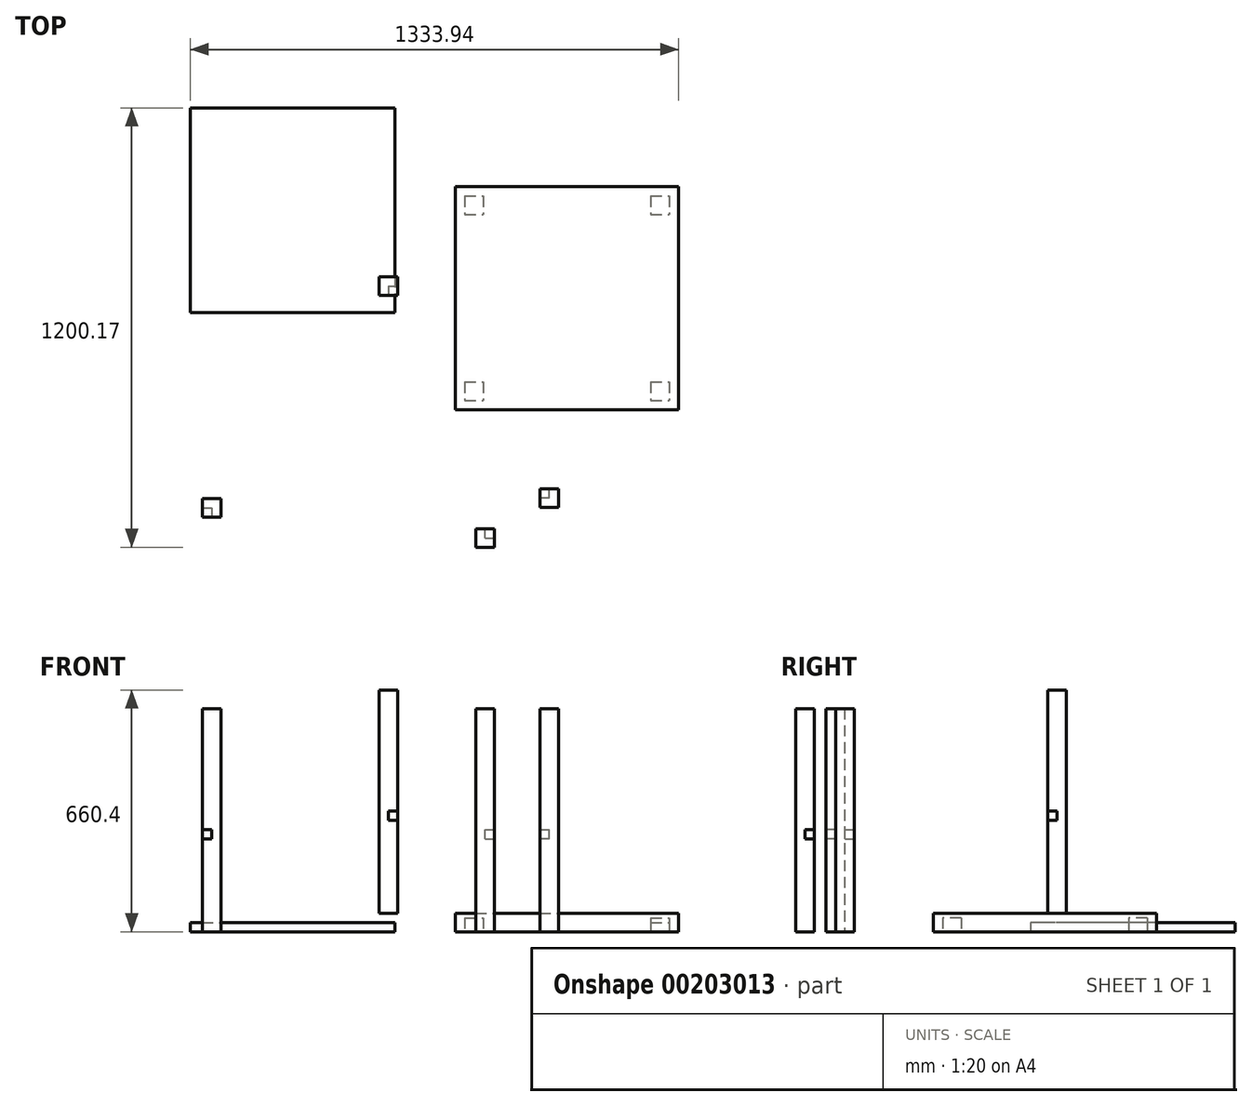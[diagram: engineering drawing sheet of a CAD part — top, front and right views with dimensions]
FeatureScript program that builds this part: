
annotation { "Feature Type Name" : "Feature", "Feature Type Description" : "" }
export const myFeature = defineFeature(function(context is Context, id is Id, definition is map)
    precondition{}
    {
        {
            var Q0;
            Q0=qCreatedBy(makeId("Top.planeOp"),FACE);
            var sketch = newSketch(context, id + "F0", { "sketchPlane" : qUnion([Q0])});
            skLineSegment(sketch, "E0.bottom", {"start": v(-297.35, 431.95) * mm, "end": v(312.25, 431.95) * mm});
            skLineSegment(sketch, "E0.top", {"start": v(-297.35, -177.65) * mm, "end": v(312.25, -177.65) * mm});
            skLineSegment(sketch, "E0.left", {"start": v(-297.35, 431.95) * mm, "end": v(-297.35, -177.65) * mm});
            skLineSegment(sketch, "E0.right", {"start": v(312.25, 431.95) * mm, "end": v(312.25, -177.65) * mm});
            skLineSegment(sketch, "E1.0", {"start": v(-297.35, 406.55) * mm, "end": v(312.25, 406.55) * mm});
            skLineSegment(sketch, "E2.0", {"start": v(286.85, 431.95) * mm, "end": v(286.85, -177.65) * mm});
            skLineSegment(sketch, "E3.0", {"start": v(-297.35, -152.25) * mm, "end": v(312.25, -152.25) * mm});
            skLineSegment(sketch, "E4.0", {"start": v(-271.95, 431.95) * mm, "end": v(-271.95, -177.65) * mm});
            skLineSegment(sketch, "E5.0", {"start": v(-297.35, 355.75) * mm, "end": v(312.25, 355.75) * mm});
            skLineSegment(sketch, "E6.0", {"start": v(236.05, 431.95) * mm, "end": v(236.05, -177.65) * mm});
            skLineSegment(sketch, "E7.0", {"start": v(-297.35, -101.45) * mm, "end": v(312.25, -101.45) * mm});
            skLineSegment(sketch, "E8.0", {"start": v(-221.15, 431.95) * mm, "end": v(-221.15, -177.65) * mm});
            skSolve(sketch);
        }
        {
            var Q0;
            {var subQ0=sQuery(id+"F0.wireOp",EDGE,"E0.left");var subQ1=sQuery(id+"F0.wireOp",EDGE,"E0.bottom");var subQ2=makeQuery(id+"F0.imprint","INTERSECT",VERTEX,{"derivedFrom":[subQ1,subQ0]});Q0=makeQuery(id+"F0.imprint","IMPRINT",FACE,{"disambiguationData":[TD([[makeQuery(id+"F0.imprint","IMPRINT",EDGE,{"disambiguationData":[TD([[subQ2,-1.0]])],"derivedFrom":subQ1}),-1.0]])]});}
            var Q1;
            {var subQ0=sQuery(id+"F0.wireOp",EDGE,"E0.right");var subQ1=sQuery(id+"F0.wireOp",EDGE,"E0.bottom");var subQ2=makeQuery(id+"F0.imprint","INTERSECT",VERTEX,{"derivedFrom":[subQ1,subQ0]});Q1=makeQuery(id+"F0.imprint","IMPRINT",FACE,{"disambiguationData":[TD([[makeQuery(id+"F0.imprint","IMPRINT",EDGE,{"disambiguationData":[TD([[subQ2,1.0]])],"derivedFrom":subQ1}),-1.0]])]});}
            var Q2;
            {var subQ0=sQuery(id+"F0.wireOp",EDGE,"E0.left");var subQ1=sQuery(id+"F0.wireOp",EDGE,"E0.top");var subQ2=makeQuery(id+"F0.imprint","INTERSECT",VERTEX,{"derivedFrom":[subQ1,subQ0]});Q2=makeQuery(id+"F0.imprint","IMPRINT",FACE,{"disambiguationData":[TD([[makeQuery(id+"F0.imprint","IMPRINT",EDGE,{"disambiguationData":[TD([[subQ2,-1.0]])],"derivedFrom":subQ1}),1.0]])]});}
            var Q3;
            {var subQ0=sQuery(id+"F0.wireOp",EDGE,"E0.right");var subQ1=sQuery(id+"F0.wireOp",EDGE,"E0.top");var subQ2=makeQuery(id+"F0.imprint","INTERSECT",VERTEX,{"derivedFrom":[subQ1,subQ0]});Q3=makeQuery(id+"F0.imprint","IMPRINT",FACE,{"disambiguationData":[TD([[makeQuery(id+"F0.imprint","IMPRINT",EDGE,{"disambiguationData":[TD([[subQ2,1.0]])],"derivedFrom":subQ1}),1.0]])]});}
            var Q4;
            {var subQ0=sQuery(id+"F0.wireOp",EDGE,"E4.0");var subQ1=sQuery(id+"F0.wireOp",EDGE,"E0.bottom");var subQ2=makeQuery(id+"F0.imprint","INTERSECT",VERTEX,{"derivedFrom":[subQ1,subQ0]});Q4=makeQuery(id+"F0.imprint","IMPRINT",FACE,{"disambiguationData":[TD([[makeQuery(id+"F0.imprint","IMPRINT",EDGE,{"disambiguationData":[TD([[subQ2,-1.0]])],"derivedFrom":subQ1}),-1.0]])]});}
            var Q5;
            {var subQ0=sQuery(id+"F0.wireOp",EDGE,"E6.0");var subQ1=sQuery(id+"F0.wireOp",EDGE,"E0.bottom");var subQ2=makeQuery(id+"F0.imprint","INTERSECT",VERTEX,{"derivedFrom":[subQ1,subQ0]});Q5=makeQuery(id+"F0.imprint","IMPRINT",FACE,{"disambiguationData":[TD([[makeQuery(id+"F0.imprint","IMPRINT",EDGE,{"disambiguationData":[TD([[subQ2,1.0]])],"derivedFrom":subQ1}),-1.0]])]});}
            var Q6;
            {var subQ0=sQuery(id+"F0.wireOp",EDGE,"E2.0");var subQ1=sQuery(id+"F0.wireOp",EDGE,"E0.bottom");var subQ2=makeQuery(id+"F0.imprint","INTERSECT",VERTEX,{"derivedFrom":[subQ1,subQ0]});Q6=makeQuery(id+"F0.imprint","IMPRINT",FACE,{"disambiguationData":[TD([[makeQuery(id+"F0.imprint","IMPRINT",EDGE,{"disambiguationData":[TD([[subQ2,1.0]])],"derivedFrom":subQ1}),-1.0]])]});}
            var Q7;
            {var subQ0=sQuery(id+"F0.wireOp",EDGE,"E4.0");var subQ1=sQuery(id+"F0.wireOp",EDGE,"E0.top");var subQ2=makeQuery(id+"F0.imprint","INTERSECT",VERTEX,{"derivedFrom":[subQ1,subQ0]});Q7=makeQuery(id+"F0.imprint","IMPRINT",FACE,{"disambiguationData":[TD([[makeQuery(id+"F0.imprint","IMPRINT",EDGE,{"disambiguationData":[TD([[subQ2,-1.0]])],"derivedFrom":subQ1}),1.0]])]});}
            var Q8;
            {var subQ0=sQuery(id+"F0.wireOp",EDGE,"E6.0");var subQ1=sQuery(id+"F0.wireOp",EDGE,"E0.top");var subQ2=makeQuery(id+"F0.imprint","INTERSECT",VERTEX,{"derivedFrom":[subQ1,subQ0]});Q8=makeQuery(id+"F0.imprint","IMPRINT",FACE,{"disambiguationData":[TD([[makeQuery(id+"F0.imprint","IMPRINT",EDGE,{"disambiguationData":[TD([[subQ2,1.0]])],"derivedFrom":subQ1}),1.0]])]});}
            var Q9;
            {var subQ0=sQuery(id+"F0.wireOp",EDGE,"E2.0");var subQ1=sQuery(id+"F0.wireOp",EDGE,"E0.top");var subQ2=makeQuery(id+"F0.imprint","INTERSECT",VERTEX,{"derivedFrom":[subQ1,subQ0]});Q9=makeQuery(id+"F0.imprint","IMPRINT",FACE,{"disambiguationData":[TD([[makeQuery(id+"F0.imprint","IMPRINT",EDGE,{"disambiguationData":[TD([[subQ2,1.0]])],"derivedFrom":subQ1}),1.0]])]});}
            var Q10;
            {var subQ0=sQuery(id+"F0.wireOp",EDGE,"E1.0");var subQ1=sQuery(id+"F0.wireOp",EDGE,"E0.left");var subQ2=makeQuery(id+"F0.imprint","INTERSECT",VERTEX,{"derivedFrom":[subQ1,subQ0]});Q10=makeQuery(id+"F0.imprint","IMPRINT",FACE,{"disambiguationData":[TD([[makeQuery(id+"F0.imprint","IMPRINT",EDGE,{"disambiguationData":[TD([[subQ2,-1.0]])],"derivedFrom":subQ1}),1.0]])]});}
            var Q11;
            {var subQ0=sQuery(id+"F0.wireOp",EDGE,"E5.0");var subQ1=sQuery(id+"F0.wireOp",EDGE,"E0.left");var subQ2=makeQuery(id+"F0.imprint","INTERSECT",VERTEX,{"derivedFrom":[subQ1,subQ0]});Q11=makeQuery(id+"F0.imprint","IMPRINT",FACE,{"disambiguationData":[TD([[makeQuery(id+"F0.imprint","IMPRINT",EDGE,{"disambiguationData":[TD([[subQ2,-1.0]])],"derivedFrom":subQ1}),1.0]])]});}
            var Q12;
            {var subQ0=sQuery(id+"F0.wireOp",EDGE,"E3.0");var subQ1=sQuery(id+"F0.wireOp",EDGE,"E0.left");var subQ2=makeQuery(id+"F0.imprint","INTERSECT",VERTEX,{"derivedFrom":[subQ1,subQ0]});Q12=makeQuery(id+"F0.imprint","IMPRINT",FACE,{"disambiguationData":[TD([[makeQuery(id+"F0.imprint","IMPRINT",EDGE,{"disambiguationData":[TD([[subQ2,1.0]])],"derivedFrom":subQ1}),1.0]])]});}
            var Q13;
            {var subQ0=sQuery(id+"F0.wireOp",EDGE,"E1.0");var subQ1=sQuery(id+"F0.wireOp",EDGE,"E0.right");var subQ2=makeQuery(id+"F0.imprint","INTERSECT",VERTEX,{"derivedFrom":[subQ1,subQ0]});Q13=makeQuery(id+"F0.imprint","IMPRINT",FACE,{"disambiguationData":[TD([[makeQuery(id+"F0.imprint","IMPRINT",EDGE,{"disambiguationData":[TD([[subQ2,-1.0]])],"derivedFrom":subQ1}),-1.0]])]});}
            var Q14;
            {var subQ0=sQuery(id+"F0.wireOp",EDGE,"E5.0");var subQ1=sQuery(id+"F0.wireOp",EDGE,"E0.right");var subQ2=makeQuery(id+"F0.imprint","INTERSECT",VERTEX,{"derivedFrom":[subQ1,subQ0]});Q14=makeQuery(id+"F0.imprint","IMPRINT",FACE,{"disambiguationData":[TD([[makeQuery(id+"F0.imprint","IMPRINT",EDGE,{"disambiguationData":[TD([[subQ2,-1.0]])],"derivedFrom":subQ1}),-1.0]])]});}
            var Q15;
            {var subQ0=sQuery(id+"F0.wireOp",EDGE,"E3.0");var subQ1=sQuery(id+"F0.wireOp",EDGE,"E0.right");var subQ2=makeQuery(id+"F0.imprint","INTERSECT",VERTEX,{"derivedFrom":[subQ1,subQ0]});Q15=makeQuery(id+"F0.imprint","IMPRINT",FACE,{"disambiguationData":[TD([[makeQuery(id+"F0.imprint","IMPRINT",EDGE,{"disambiguationData":[TD([[subQ2,1.0]])],"derivedFrom":subQ1}),-1.0]])]});}
            var Q16;
            {var subQ0=sQuery(id+"F0.wireOp",EDGE,"E5.0");var subQ1=sQuery(id+"F0.wireOp",EDGE,"E4.0");var subQ2=makeQuery(id+"F0.imprint","INTERSECT",VERTEX,{"derivedFrom":[subQ1,subQ0]});Q16=makeQuery(id+"F0.imprint","IMPRINT",FACE,{"disambiguationData":[TD([[makeQuery(id+"F0.imprint","IMPRINT",EDGE,{"disambiguationData":[TD([[subQ2,-1.0]])],"derivedFrom":subQ1}),1.0]])]});}
            var Q17;
            {var subQ0=sQuery(id+"F0.wireOp",EDGE,"E8.0");var subQ1=sQuery(id+"F0.wireOp",EDGE,"E1.0");var subQ2=makeQuery(id+"F0.imprint","INTERSECT",VERTEX,{"derivedFrom":[subQ1,subQ0]});Q17=makeQuery(id+"F0.imprint","IMPRINT",FACE,{"disambiguationData":[TD([[makeQuery(id+"F0.imprint","IMPRINT",EDGE,{"disambiguationData":[TD([[subQ2,-1.0]])],"derivedFrom":subQ1}),-1.0]])]});}
            var Q18;
            {var subQ0=sQuery(id+"F0.wireOp",EDGE,"E5.0");var subQ1=sQuery(id+"F0.wireOp",EDGE,"E2.0");var subQ2=makeQuery(id+"F0.imprint","INTERSECT",VERTEX,{"derivedFrom":[subQ1,subQ0]});Q18=makeQuery(id+"F0.imprint","IMPRINT",FACE,{"disambiguationData":[TD([[makeQuery(id+"F0.imprint","IMPRINT",EDGE,{"disambiguationData":[TD([[subQ2,-1.0]])],"derivedFrom":subQ1}),-1.0]])]});}
            var Q19;
            {var subQ0=sQuery(id+"F0.wireOp",EDGE,"E4.0");var subQ1=sQuery(id+"F0.wireOp",EDGE,"E1.0");var subQ2=makeQuery(id+"F0.imprint","INTERSECT",VERTEX,{"derivedFrom":[subQ1,subQ0]});Q19=makeQuery(id+"F0.imprint","IMPRINT",FACE,{"disambiguationData":[TD([[makeQuery(id+"F0.imprint","IMPRINT",EDGE,{"disambiguationData":[TD([[subQ2,-1.0]])],"derivedFrom":subQ1}),-1.0]])]});}
            var Q20;
            {var subQ0=sQuery(id+"F0.wireOp",EDGE,"E4.0");var subQ1=sQuery(id+"F0.wireOp",EDGE,"E3.0");var subQ2=makeQuery(id+"F0.imprint","INTERSECT",VERTEX,{"derivedFrom":[subQ1,subQ0]});Q20=makeQuery(id+"F0.imprint","IMPRINT",FACE,{"disambiguationData":[TD([[makeQuery(id+"F0.imprint","IMPRINT",EDGE,{"disambiguationData":[TD([[subQ2,-1.0]])],"derivedFrom":subQ1}),1.0]])]});}
            var Q21;
            {var subQ0=sQuery(id+"F0.wireOp",EDGE,"E8.0");var subQ1=sQuery(id+"F0.wireOp",EDGE,"E5.0");var subQ2=makeQuery(id+"F0.imprint","INTERSECT",VERTEX,{"derivedFrom":[subQ1,subQ0]});Q21=makeQuery(id+"F0.imprint","IMPRINT",FACE,{"disambiguationData":[TD([[makeQuery(id+"F0.imprint","IMPRINT",EDGE,{"disambiguationData":[TD([[subQ2,-1.0]])],"derivedFrom":subQ1}),-1.0]])]});}
            var Q22;
            {var subQ0=sQuery(id+"F0.wireOp",EDGE,"E8.0");var subQ1=sQuery(id+"F0.wireOp",EDGE,"E3.0");var subQ2=makeQuery(id+"F0.imprint","INTERSECT",VERTEX,{"derivedFrom":[subQ1,subQ0]});Q22=makeQuery(id+"F0.imprint","IMPRINT",FACE,{"disambiguationData":[TD([[makeQuery(id+"F0.imprint","IMPRINT",EDGE,{"disambiguationData":[TD([[subQ2,-1.0]])],"derivedFrom":subQ1}),1.0]])]});}
            var Q23;
            {var subQ0=sQuery(id+"F0.wireOp",EDGE,"E7.0");var subQ1=sQuery(id+"F0.wireOp",EDGE,"E2.0");var subQ2=makeQuery(id+"F0.imprint","INTERSECT",VERTEX,{"derivedFrom":[subQ1,subQ0]});Q23=makeQuery(id+"F0.imprint","IMPRINT",FACE,{"disambiguationData":[TD([[makeQuery(id+"F0.imprint","IMPRINT",EDGE,{"disambiguationData":[TD([[subQ2,-1.0]])],"derivedFrom":subQ1}),-1.0]])]});}
            var Q24;
            {var subQ0=sQuery(id+"F0.wireOp",EDGE,"E6.0");var subQ1=sQuery(id+"F0.wireOp",EDGE,"E1.0");var subQ2=makeQuery(id+"F0.imprint","INTERSECT",VERTEX,{"derivedFrom":[subQ1,subQ0]});Q24=makeQuery(id+"F0.imprint","IMPRINT",FACE,{"disambiguationData":[TD([[makeQuery(id+"F0.imprint","IMPRINT",EDGE,{"disambiguationData":[TD([[subQ2,-1.0]])],"derivedFrom":subQ1}),-1.0]])]});}
            extrude(context, id + "F1", {"entities" : qUnion([Q0, Q1, Q2, Q3, Q4, Q5, Q6, Q7, Q8, Q9, Q10, Q11, Q12, Q13, Q14, Q15, Q16, Q17, Q18, Q19, Q20, Q21, Q22, Q23, Q24]), "depth" : 50.8 * mm});
        }
        {
            var Q0;
            {var subQ0=sQuery(id+"F0.wireOp",EDGE,"E4.0");var subQ1=sQuery(id+"F0.wireOp",EDGE,"E3.0");var subQ2=makeQuery(id+"F0.imprint","INTERSECT",VERTEX,{"derivedFrom":[subQ1,subQ0]});Q0=makeQuery(id+"F0.imprint","IMPRINT",FACE,{"disambiguationData":[TD([[makeQuery(id+"F0.imprint","IMPRINT",EDGE,{"disambiguationData":[TD([[subQ2,-1.0]])],"derivedFrom":subQ1}),1.0]])]});}
            extrude(context, id + "F2", {"entities" : qUnion([Q0]), "operationType" : NewBodyOperationType.REMOVE, "oppositeDirection" : true, "depth" : 38.1 * mm});
        }
        {
            var Q0;
            {var subQ0=sQuery(id+"F0.wireOp",EDGE,"E4.0");var subQ1=sQuery(id+"F0.wireOp",EDGE,"E3.0");var subQ2=makeQuery(id+"F0.imprint","INTERSECT",VERTEX,{"derivedFrom":[subQ1,subQ0]});Q0=makeQuery(id+"F0.imprint","IMPRINT",FACE,{"disambiguationData":[TD([[makeQuery(id+"F0.imprint","IMPRINT",EDGE,{"disambiguationData":[TD([[subQ2,-1.0]])],"derivedFrom":subQ1}),1.0]])]});}
            extrude(context, id + "F3", {"entities" : qUnion([Q0]), "operationType" : NewBodyOperationType.REMOVE, "depth" : 38.1 * mm});
        }
        {
            var Q0;
            {var subQ0=sQuery(id+"F0.wireOp",EDGE,"E7.0");var subQ1=sQuery(id+"F0.wireOp",EDGE,"E2.0");var subQ2=makeQuery(id+"F0.imprint","INTERSECT",VERTEX,{"derivedFrom":[subQ1,subQ0]});Q0=makeQuery(id+"F0.imprint","IMPRINT",FACE,{"disambiguationData":[TD([[makeQuery(id+"F0.imprint","IMPRINT",EDGE,{"disambiguationData":[TD([[subQ2,-1.0]])],"derivedFrom":subQ1}),-1.0]])]});}
            extrude(context, id + "F4", {"entities" : qUnion([Q0]), "operationType" : NewBodyOperationType.REMOVE, "depth" : 38.1 * mm});
        }
        {
            var Q0;
            {var subQ0=sQuery(id+"F0.wireOp",EDGE,"E4.0");var subQ1=sQuery(id+"F0.wireOp",EDGE,"E1.0");var subQ2=makeQuery(id+"F0.imprint","INTERSECT",VERTEX,{"derivedFrom":[subQ1,subQ0]});Q0=makeQuery(id+"F0.imprint","IMPRINT",FACE,{"disambiguationData":[TD([[makeQuery(id+"F0.imprint","IMPRINT",EDGE,{"disambiguationData":[TD([[subQ2,-1.0]])],"derivedFrom":subQ1}),-1.0]])]});}
            extrude(context, id + "F5", {"entities" : qUnion([Q0]), "operationType" : NewBodyOperationType.REMOVE, "depth" : 38.1 * mm});
        }
        {
            var Q0;
            Q0=makeQuery(id+"F1.opExtrude","CAP_FACE",FACE,{"disambiguationData":[OSD([sQuery(id+"F0.wireOp",EDGE,"E0.bottom"),sQuery(id+"F0.wireOp",EDGE,"E0.top"),sQuery(id+"F0.wireOp",EDGE,"E0.left"),sQuery(id+"F0.wireOp",EDGE,"E0.right")])],"isStart":false});
            var sketch = newSketch(context, id + "F6", { "sketchPlane" : qUnion([Q0])});
            skLineSegment(sketch, "E9.bottom", {"start": v(-506.38, 185.9) * mm, "end": v(-455.58, 185.9) * mm});
            skLineSegment(sketch, "E9.top", {"start": v(-506.38, 135.1) * mm, "end": v(-455.58, 135.1) * mm});
            skLineSegment(sketch, "E9.left", {"start": v(-506.38, 185.9) * mm, "end": v(-506.38, 135.1) * mm});
            skLineSegment(sketch, "E9.right", {"start": v(-455.58, 185.9) * mm, "end": v(-455.58, 135.1) * mm});
            skLineSegment(sketch, "E10.0", {"start": v(-506.38, 160.5) * mm, "end": v(-455.58, 160.5) * mm});
            skLineSegment(sketch, "E11.0", {"start": v(-480.98, 185.9) * mm, "end": v(-480.98, 135.1) * mm});
            skSolve(sketch);
        }
        {
            var Q0;
            Q0 = qSketchRegion(id + "F6", true);
            extrude(context, id + "F7", {"entities" : qUnion([Q0]), "depth" : 609.6 * mm});
        }
        {
            var Q0;
            Q0=qCreatedBy(makeId("Top.planeOp"),FACE);
            var sketch = newSketch(context, id + "F8", { "sketchPlane" : qUnion([Q0])});
            skLineSegment(sketch, "E12.bottom", {"start": v(-242.21, -501.92) * mm, "end": v(-191.41, -501.92) * mm});
            skLineSegment(sketch, "E12.top", {"start": v(-242.21, -552.72) * mm, "end": v(-191.41, -552.72) * mm});
            skLineSegment(sketch, "E12.left", {"start": v(-242.21, -501.92) * mm, "end": v(-242.21, -552.72) * mm});
            skLineSegment(sketch, "E12.right", {"start": v(-191.41, -501.92) * mm, "end": v(-191.41, -552.72) * mm});
            skLineSegment(sketch, "E13.0", {"start": v(-242.21, -527.32) * mm, "end": v(-191.41, -527.32) * mm});
            skLineSegment(sketch, "E14.0", {"start": v(-216.81, -501.92) * mm, "end": v(-216.81, -552.72) * mm});
            skSolve(sketch);
        }
        {
            var Q0;
            Q0=makeQuery(id+"F8.imprint","IMPRINT",FACE,{"disambiguationData":[TD([[makeQuery(id+"F8.imprint","IMPRINT",EDGE,{"derivedFrom":sQuery(id+"F8.wireOp",EDGE,"E12.bottom")}),-1.0]])]});
            extrude(context, id + "F9", {"entities" : qUnion([Q0]), "operationType" : NewBodyOperationType.ADD, "depth" : 609.6 * mm});
        }
        {
            var Q0;
            Q0 = qSketchRegion(id + "F8", true);
            extrude(context, id + "F10", {"entities" : qUnion([Q0]), "operationType" : NewBodyOperationType.ADD, "depth" : 609.6 * mm});
        }
        {
            var Q0;
            Q0=qCreatedBy(makeId("Top.planeOp"),FACE);
            var sketch = newSketch(context, id + "F11", { "sketchPlane" : qUnion([Q0])});
            skLineSegment(sketch, "E15.bottom", {"start": v(-989.34, -521.4) * mm, "end": v(-938.54, -521.4) * mm});
            skLineSegment(sketch, "E15.top", {"start": v(-989.34, -470.6) * mm, "end": v(-938.54, -470.6) * mm});
            skLineSegment(sketch, "E15.left", {"start": v(-989.34, -521.4) * mm, "end": v(-989.34, -470.6) * mm});
            skLineSegment(sketch, "E15.right", {"start": v(-938.54, -521.4) * mm, "end": v(-938.54, -470.6) * mm});
            skLineSegment(sketch, "E16.0", {"start": v(-963.94, -521.4) * mm, "end": v(-963.94, -470.6) * mm});
            skLineSegment(sketch, "E17.0", {"start": v(-989.34, -496) * mm, "end": v(-938.54, -496) * mm});
            skSolve(sketch);
        }
        {
            var Q0;
            Q0 = qSketchRegion(id + "F11", true);
            extrude(context, id + "F12", {"entities" : qUnion([Q0]), "operationType" : NewBodyOperationType.ADD, "depth" : 609.6 * mm});
        }
        {
            var Q0;
            Q0=qCreatedBy(makeId("Top.planeOp"),FACE);
            var sketch = newSketch(context, id + "F13", { "sketchPlane" : qUnion([Q0])});
            skLineSegment(sketch, "E18.bottom", {"start": v(-31.1, -378.64) * mm, "end": v(19.7, -378.64) * mm});
            skLineSegment(sketch, "E18.top", {"start": v(-31.1, -429.44) * mm, "end": v(19.7, -429.44) * mm});
            skLineSegment(sketch, "E18.left", {"start": v(-31.1, -378.64) * mm, "end": v(-31.1, -429.44) * mm});
            skLineSegment(sketch, "E18.right", {"start": v(19.7, -378.64) * mm, "end": v(19.7, -429.44) * mm});
            skLineSegment(sketch, "E19.0", {"start": v(-31.1, -404.04) * mm, "end": v(19.7, -404.04) * mm});
            skLineSegment(sketch, "E20.0", {"start": v(-5.7, -378.64) * mm, "end": v(-5.7, -429.44) * mm});
            skSolve(sketch);
        }
        {
            var Q0;
            Q0 = qSketchRegion(id + "F13", true);
            extrude(context, id + "F14", {"entities" : qUnion([Q0]), "operationType" : NewBodyOperationType.ADD, "depth" : 609.6 * mm});
        }
        {
            var Q0;
            {var subQ0=sQuery(id+"F13.wireOp",EDGE,"E18.left");var subQ1=sQuery(id+"F13.wireOp",EDGE,"E18.top");var subQ2=makeQuery(id+"F13.imprint","INTERSECT",VERTEX,{"derivedFrom":[subQ1,subQ0]});Q0=makeQuery(id+"F13.imprint","IMPRINT",FACE,{"disambiguationData":[TD([[makeQuery(id+"F13.imprint","IMPRINT",EDGE,{"disambiguationData":[TD([[subQ2,-1.0]])],"derivedFrom":subQ1}),1.0]])]});}
            extrude(context, id + "F15", {"entities" : qUnion([Q0]), "operationType" : NewBodyOperationType.ADD, "depth" : 609.6 * mm});
        }
        {
            var Q0;
            Q0=qCreatedBy(makeId("Top.planeOp"),FACE);
            var sketch = newSketch(context, id + "F16", { "sketchPlane" : qUnion([Q0])});
            skLineSegment(sketch, "E21.bottom", {"start": v(-1021.69, 647.45) * mm, "end": v(-462.89, 647.45) * mm});
            skLineSegment(sketch, "E21.top", {"start": v(-1021.69, 88.65) * mm, "end": v(-462.89, 88.65) * mm});
            skLineSegment(sketch, "E21.left", {"start": v(-1021.69, 647.45) * mm, "end": v(-1021.69, 88.65) * mm});
            skLineSegment(sketch, "E21.right", {"start": v(-462.89, 647.45) * mm, "end": v(-462.89, 88.65) * mm});
            skSolve(sketch);
        }
        {
            var Q0;
            Q0 = qSketchRegion(id + "F16", true);
            extrude(context, id + "F17", {"entities" : qUnion([Q0]), "operationType" : NewBodyOperationType.ADD, "depth" : 25.4 * mm});
        }
        {
            var Q0;
            Q0=makeQuery(id+"F12.opExtrude","SWEPT_FACE",FACE,{"disambiguationData":[OSD([sQuery(id+"F11.wireOp",EDGE,"E15.right")])]});
            var sketch = newSketch(context, id + "F18", { "sketchPlane" : qUnion([Q0])});
            skLineSegment(sketch, "E22.0", {"start": v(-521.4, 279.4) * mm, "end": v(-470.6, 279.4) * mm});
            skLineSegment(sketch, "E23.0", {"start": v(-521.4, 254) * mm, "end": v(-470.6, 254) * mm});
            skLineSegment(sketch, "E24.0", {"start": v(-496, 609.6) * mm, "end": v(-496, 0) * mm});
            skSolve(sketch);
        }
        {
            var Q0;
            {var subQ0=sQuery(id+"F18.wireOp",EDGE,"E22.0");var subQ3=sQuery(id+"F18.wireOp",EDGE,"E24.0");var subQ4=makeQuery(id+"F18.imprint","INTERSECT",VERTEX,{"derivedFrom":[subQ0,subQ3]});Q0=makeQuery(id+"F18.imprint","IMPRINT",FACE,{"disambiguationData":[TD([[makeQuery(id+"F18.imprint","IMPRINT",EDGE,{"disambiguationData":[TD([[subQ4,-1.0]])],"derivedFrom":subQ3}),-1.0]])]});}
            extrude(context, id + "F19", {"entities" : qUnion([Q0]), "operationType" : NewBodyOperationType.REMOVE, "oppositeDirection" : true, "depth" : 25.4 * mm});
        }
        {
            var Q0;
            {var subQ0=sQuery(id+"F8.wireOp",EDGE,"E12.right");Q0=makeQuery(id+"F10.boolean.opBoolean","MERGE",FACE,{"derivedFrom":[makeQuery(id+"F9.opExtrude","SWEPT_FACE",FACE,{"disambiguationData":[OSD([subQ0])]}),makeQuery(id+"F10.opExtrude","SWEPT_FACE",FACE,{"disambiguationData":[OSD([subQ0])]})]});}
            var Q1;
            Q1 = qBodyType(qCreatedBy(id + "FpB0nm8VUIwHlho_5" ,EDGE), BodyType.WIRE);
            cPlane(context, id + "F20", {"entities" : qUnion([Q0, Q1]), "cplaneType" : CPlaneType.OFFSET, "offset" : 0 * mm, "oppositeDirection" : true, "width" : 152.4 * mm, "height" : 152.4 * mm});
        }
        {
            var Q0;
            Q0=qCreatedBy(id+"F20.planeOp",FACE);
            var sketch = newSketch(context, id + "F21", { "sketchPlane" : qUnion([Q0])});
            skLineSegment(sketch, "E25.0.0", {"start": v(-552.72, 0) * mm, "end": v(-501.92, 0) * mm});
            skLineSegment(sketch, "E25.0.1", {"start": v(-501.92, 0) * mm, "end": v(-501.92, 609.6) * mm});
            skLineSegment(sketch, "E25.0.2", {"start": v(-501.92, 609.6) * mm, "end": v(-552.72, 609.6) * mm});
            skLineSegment(sketch, "E25.0.3", {"start": v(-552.72, 609.6) * mm, "end": v(-552.72, 0) * mm});
            skLineSegment(sketch, "E26.0", {"start": v(-501.92, 279.4) * mm, "end": v(-552.72, 279.4) * mm});
            skLineSegment(sketch, "E27.0", {"start": v(-552.72, 254) * mm, "end": v(-501.92, 254) * mm});
            skLineSegment(sketch, "E28.0", {"start": v(-527.32, 609.6) * mm, "end": v(-527.32, 0) * mm});
            skSolve(sketch);
        }
        {
            var Q0;
            {var subQ0=sQuery(id+"F21.wireOp",EDGE,"E26.0");var subQ1=sQuery(id+"F21.wireOp",EDGE,"E25.0.1");var subQ2=makeQuery(id+"F21.imprint","INTERSECT",VERTEX,{"derivedFrom":[subQ1,subQ0]});Q0=makeQuery(id+"F21.imprint","IMPRINT",FACE,{"disambiguationData":[TD([[makeQuery(id+"F21.imprint","IMPRINT",EDGE,{"disambiguationData":[TD([[subQ2,1.0]])],"derivedFrom":subQ1}),1.0]])]});}
            extrude(context, id + "F22", {"entities" : qUnion([Q0]), "operationType" : NewBodyOperationType.REMOVE, "oppositeDirection" : true, "depth" : 25.4 * mm});
        }
        {
            var Q0;
            Q0=makeQuery(id+"F14.opExtrude","SWEPT_FACE",FACE,{"disambiguationData":[OSD([sQuery(id+"F13.wireOp",EDGE,"E18.top")])]});
            cPlane(context, id + "F23", {"entities" : qUnion([Q0]), "cplaneType" : CPlaneType.OFFSET, "offset" : 0 * mm, "oppositeDirection" : true, "width" : 152.4 * mm, "height" : 152.4 * mm});
        }
        {
            var Q0;
            Q0=qCreatedBy(id+"F23.planeOp",FACE);
            var sketch = newSketch(context, id + "F24", { "sketchPlane" : qUnion([Q0])});
            skLineSegment(sketch, "E29.0.0", {"start": v(19.7, 0) * mm, "end": v(19.7, 609.6) * mm});
            skLineSegment(sketch, "E29.0.1", {"start": v(19.7, 609.6) * mm, "end": v(-31.1, 609.6) * mm});
            skLineSegment(sketch, "E29.0.2", {"start": v(-31.1, 609.6) * mm, "end": v(-31.1, 0) * mm});
            skLineSegment(sketch, "E29.0.3", {"start": v(-31.1, 0) * mm, "end": v(19.7, 0) * mm});
            skLineSegment(sketch, "E30.0", {"start": v(-31.1, 254) * mm, "end": v(19.7, 254) * mm});
            skLineSegment(sketch, "E31.0", {"start": v(19.7, 279.4) * mm, "end": v(-31.1, 279.4) * mm});
            skLineSegment(sketch, "E32.0", {"start": v(-5.7, 0) * mm, "end": v(-5.7, 609.6) * mm});
            skSolve(sketch);
        }
        {
            var Q0;
            {var subQ0=sQuery(id+"F24.wireOp",EDGE,"E30.0");var subQ1=sQuery(id+"F24.wireOp",EDGE,"E29.0.0");var subQ2=makeQuery(id+"F24.imprint","INTERSECT",VERTEX,{"derivedFrom":[subQ1,subQ0]});Q0=makeQuery(id+"F24.imprint","IMPRINT",FACE,{"disambiguationData":[TD([[makeQuery(id+"F24.imprint","IMPRINT",EDGE,{"disambiguationData":[TD([[subQ2,-1.0]])],"derivedFrom":subQ1}),1.0]])]});}
            extrude(context, id + "F25", {"entities" : qUnion([Q0]), "operationType" : NewBodyOperationType.REMOVE, "oppositeDirection" : true, "depth" : 25.4 * mm});
        }
        {
            var Q0;
            Q0=makeQuery(id+"F7.opExtrude","SWEPT_FACE",FACE,{"disambiguationData":[OSD([sQuery(id+"F6.wireOp",EDGE,"E9.right")])]});
            cPlane(context, id + "F26", {"entities" : qUnion([Q0]), "cplaneType" : CPlaneType.OFFSET, "offset" : 0 * mm, "oppositeDirection" : true, "width" : 152.4 * mm, "height" : 152.4 * mm});
        }
        {
            var Q0;
            Q0=qCreatedBy(id+"F26.planeOp",FACE);
            var sketch = newSketch(context, id + "F27", { "sketchPlane" : qUnion([Q0])});
            skLineSegment(sketch, "E33.0.0", {"start": v(135.1, 50.8) * mm, "end": v(185.9, 50.8) * mm});
            skLineSegment(sketch, "E33.0.1", {"start": v(185.9, 50.8) * mm, "end": v(185.9, 660.4) * mm});
            skLineSegment(sketch, "E33.0.2", {"start": v(185.9, 660.4) * mm, "end": v(135.1, 660.4) * mm});
            skLineSegment(sketch, "E33.0.3", {"start": v(135.1, 660.4) * mm, "end": v(135.1, 50.8) * mm});
            skLineSegment(sketch, "E34.0", {"start": v(185.9, 330.2) * mm, "end": v(135.1, 330.2) * mm});
            skLineSegment(sketch, "E35.0", {"start": v(135.1, 304.8) * mm, "end": v(185.9, 304.8) * mm});
            skLineSegment(sketch, "E36.0", {"start": v(160.5, 50.8) * mm, "end": v(160.5, 660.4) * mm});
            skSolve(sketch);
        }
        {
            var Q0;
            {var subQ0=sQuery(id+"F27.wireOp",EDGE,"E34.0");var subQ1=sQuery(id+"F27.wireOp",EDGE,"E33.0.3");var subQ2=makeQuery(id+"F27.imprint","INTERSECT",VERTEX,{"derivedFrom":[subQ1,subQ0]});Q0=makeQuery(id+"F27.imprint","IMPRINT",FACE,{"disambiguationData":[TD([[makeQuery(id+"F27.imprint","IMPRINT",EDGE,{"disambiguationData":[TD([[subQ2,-1.0]])],"derivedFrom":subQ1}),1.0]])]});}
            extrude(context, id + "F28", {"entities" : qUnion([Q0]), "operationType" : NewBodyOperationType.REMOVE, "oppositeDirection" : true, "depth" : 25.4 * mm});
        }
        {
            var Q0;
            Q0=makeQuery(id+"F14.opExtrude","SWEPT_BODY",BODY,{"disambiguationData":[OSD([sQuery(id+"F13.wireOp",EDGE,"E18.bottom"),sQuery(id+"F13.wireOp",EDGE,"E18.top"),sQuery(id+"F13.wireOp",EDGE,"E18.left"),sQuery(id+"F13.wireOp",EDGE,"E18.right")])]});
            var Q1;
            {var subQ0=sQuery(id+"F13.wireOp",EDGE,"E18.right");var subQ1=sQuery(id+"F13.wireOp",EDGE,"E18.top");Q1=makeQuery(id+"F25.boolean.opBoolean","SPLIT",EDGE,{"disambiguationData":[TD([makeQuery(id+"F25.opExtrude","SWEPT_FACE",FACE,{"disambiguationData":[OSD([sQuery(id+"F24.wireOp",EDGE,"E30.0")])]})])],"derivedFrom":makeQuery(id+"F14.opExtrude","SWEPT_EDGE",EDGE,{"disambiguationData":[OSD([subQ1,subQ0])]})});}
            transform(context, id + "F29", {"entities" : qUnion([Q0]), "transformType" : TransformType.ROTATION, "transformAxis" : qUnion([Q1]), "angle" : 45 * degree, "makeCopy" : false});
        }
        {
            var Q0;
            {var subQ0=sQuery(id+"F0.wireOp",EDGE,"E6.0");var subQ1=sQuery(id+"F0.wireOp",EDGE,"E1.0");var subQ2=makeQuery(id+"F0.imprint","INTERSECT",VERTEX,{"derivedFrom":[subQ1,subQ0]});Q0=makeQuery(id+"F0.imprint","IMPRINT",FACE,{"disambiguationData":[TD([[makeQuery(id+"F0.imprint","IMPRINT",EDGE,{"disambiguationData":[TD([[subQ2,-1.0]])],"derivedFrom":subQ1}),-1.0]])]});}
            extrude(context, id + "F30", {"entities" : qUnion([Q0]), "operationType" : NewBodyOperationType.ADD, "depth" : 25.4 * mm});
        }
        {
            var Q0;
            {var subQ0=sQuery(id+"F0.wireOp",EDGE,"E6.0");var subQ1=sQuery(id+"F0.wireOp",EDGE,"E1.0");var subQ2=makeQuery(id+"F0.imprint","INTERSECT",VERTEX,{"derivedFrom":[subQ1,subQ0]});Q0=makeQuery(id+"F0.imprint","IMPRINT",FACE,{"disambiguationData":[TD([[makeQuery(id+"F0.imprint","IMPRINT",EDGE,{"disambiguationData":[TD([[subQ2,-1.0]])],"derivedFrom":subQ1}),-1.0]])]});}
            extrude(context, id + "F31", {"entities" : qUnion([Q0]), "operationType" : NewBodyOperationType.REMOVE, "depth" : 25.4 * mm});
        }
        {
            var Q0;
            Q0=makeQuery(id+"F12.opExtrude","SWEPT_BODY",BODY,{"disambiguationData":[OSD([sQuery(id+"F11.wireOp",EDGE,"E15.bottom"),sQuery(id+"F11.wireOp",EDGE,"E15.top"),sQuery(id+"F11.wireOp",EDGE,"E15.left"),sQuery(id+"F11.wireOp",EDGE,"E15.right")])]});
            var Q1;
            Q1=makeQuery(id+"F12.opExtrude","SWEPT_EDGE",EDGE,{"disambiguationData":[OSD([sQuery(id+"F11.wireOp",EDGE,"E15.top"),sQuery(id+"F11.wireOp",EDGE,"E15.right")])]});
            transform(context, id + "F32", {"entities" : qUnion([Q0]), "transformType" : TransformType.ROTATION, "transformAxis" : qUnion([Q1]), "angle" : 90 * degree, "makeCopy" : false});
        }
        {
            var Q0;
            Q0=makeQuery(id+"F14.opExtrude","SWEPT_BODY",BODY,{"disambiguationData":[OSD([sQuery(id+"F13.wireOp",EDGE,"E18.bottom"),sQuery(id+"F13.wireOp",EDGE,"E18.top"),sQuery(id+"F13.wireOp",EDGE,"E18.left"),sQuery(id+"F13.wireOp",EDGE,"E18.right")])]});
            var Q1;
            Q1=makeQuery(id+"F14.opExtrude","SWEPT_EDGE",EDGE,{"disambiguationData":[OSD([sQuery(id+"F13.wireOp",EDGE,"E18.top"),sQuery(id+"F13.wireOp",EDGE,"E18.left")])]});
            transform(context, id + "F33", {"entities" : qUnion([Q0]), "transformType" : TransformType.ROTATION, "transformAxis" : qUnion([Q1]), "angle" : 135 * degree, "makeCopy" : false});
        }
    });
